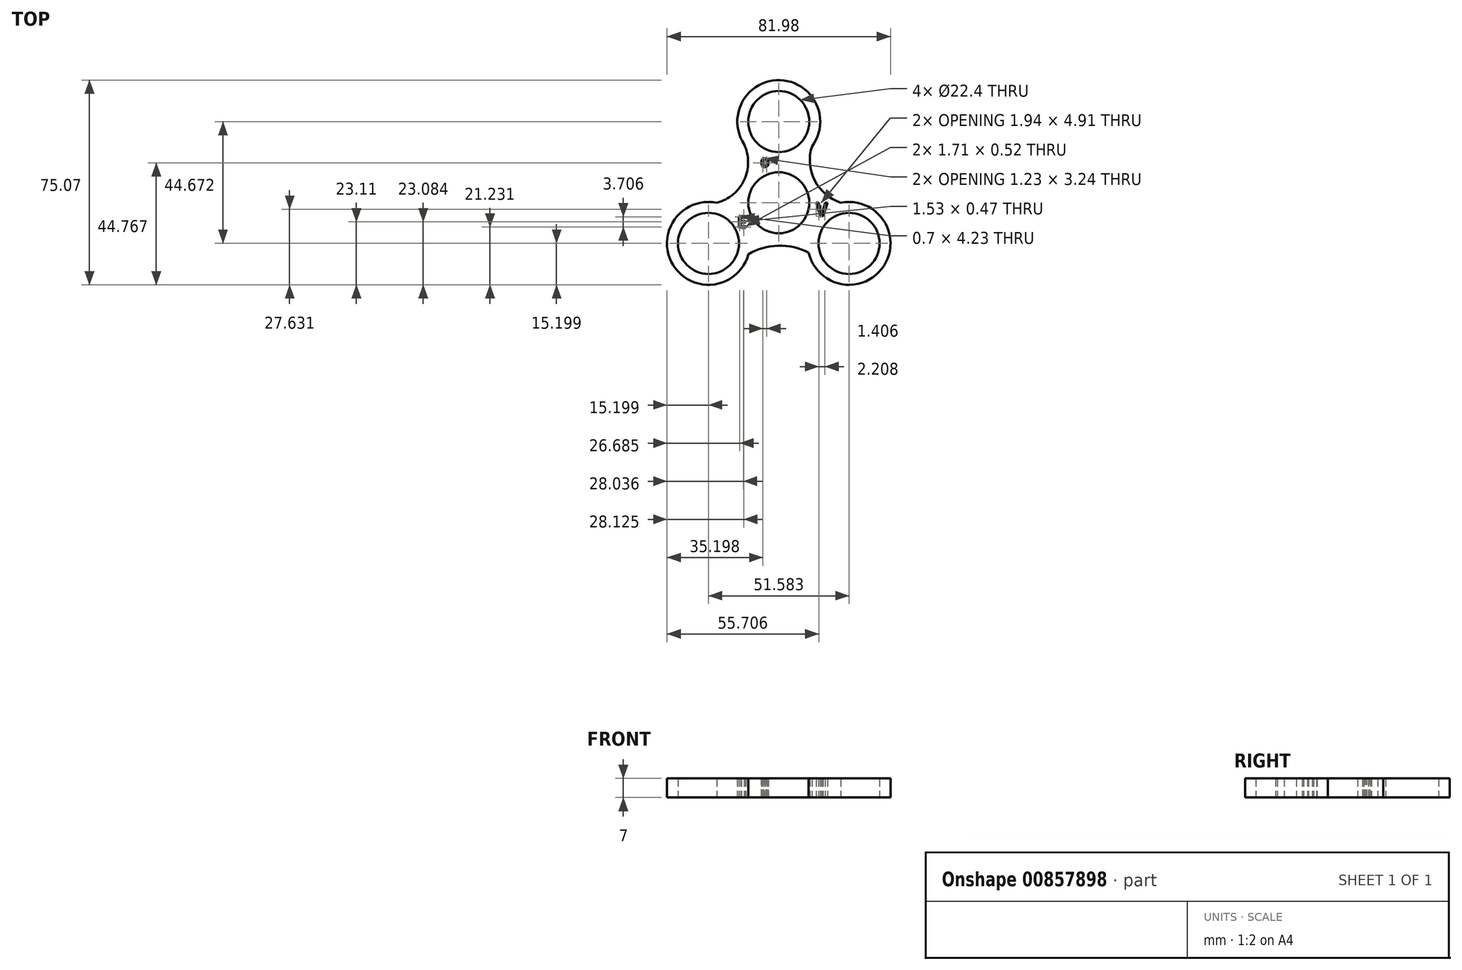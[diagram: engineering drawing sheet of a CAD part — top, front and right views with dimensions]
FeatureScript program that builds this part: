
annotation { "Feature Type Name" : "Feature", "Feature Type Description" : "" }
export const myFeature = defineFeature(function(context is Context, id is Id, definition is map)
    precondition{}
    {
        {
            var Q0;
            Q0=qCreatedBy(makeId("Top.planeOp"),FACE);
            var sketch = newSketch(context, id + "F0", { "sketchPlane" : qUnion([Q0])});
            skCircle(sketch, "E0", {"center": v(0, 0) * mm, "radius": 11.2 * mm});
            skCircle(sketch, "E1", {"center": v(0, 29.78) * mm, "radius": 11.2 * mm});
            skArc(sketch, "E2.1.0", {"start": v(-22.74, 0) * mm, "mid": v(-38.74, -22.85) * mm, "end": v(-11.13, -18.89) * mm});
            skCircle(sketch, "E2.1.1", {"center": v(-25.8, -14.9) * mm, "radius": 11.2 * mm});
            skCircle(sketch, "E2.2.1", {"center": v(25.8, -14.9) * mm, "radius": 11.2 * mm});
            skArc(sketch, "E3", {"start": v(12.15, 20.65) * mm, "mid": v(13.25, 8.17) * mm, "end": v(22.74, 0) * mm});
            skArc(sketch, "E4", {"start": v(-22.74, 0) * mm, "mid": v(-12.68, 8.38) * mm, "end": v(-12.73, 21.48) * mm});
            skArc(sketch, "E5", {"start": v(10.97, -18.26) * mm, "mid": v(-0.16, -15.72) * mm, "end": v(-11.13, -18.89) * mm});
            skArc(sketch, "E6.trimOffspring", {"start": v(12.15, 20.65) * mm, "mid": v(0.5, 44.97) * mm, "end": v(-12.73, 21.48) * mm});
            skArc(sketch, "E7.trimOffspring", {"start": v(10.97, -18.26) * mm, "mid": v(38.57, -23.13) * mm, "end": v(22.74, 0) * mm});
            skArc(sketch, "E8.trimOffspring", {"start": v(-12.7, 8.36) * mm, "mid": v(-13.27, 7.42) * mm, "end": v(-13.77, 6.43) * mm});
            skText(sketch, "E9", { "text": "O", "fontName": "AllertaStencil-Regular.ttf"});
            skText(sketch, "E10", { "text": "E", "fontName": "AllertaStencil-Regular.ttf"});
            skText(sketch, "E11", { "text": "V", "fontName": "AllertaStencil-Regular.ttf"});
            const initialGuessF0  = {"E9": [-0.00674, 0.01308, 1, 0, 0.00317], "E10": [-0.0152, -0.00912, 1, 0, 0.00423], "E11": [0.01335, -0.00489, 1, 0, 0.00489]};
            skSetInitialGuess(sketch, initialGuessF0);
            skSolve(sketch);
        }
        {
            var Q0;
            Q0=makeQuery(id+"F0.imprint","IMPRINT",FACE,{"disambiguationData":[TD([[makeQuery(id+"F0.imprint","IMPRINT",EDGE,{"derivedFrom":sQuery(id+"F0.wireOp",EDGE,"E0")}),-1.0]])]});
            extrude(context, id + "F1", {"entities" : qUnion([Q0]), "depth" : 7 * mm, "offsetDistance" : 25 * mm});
        }
    });
